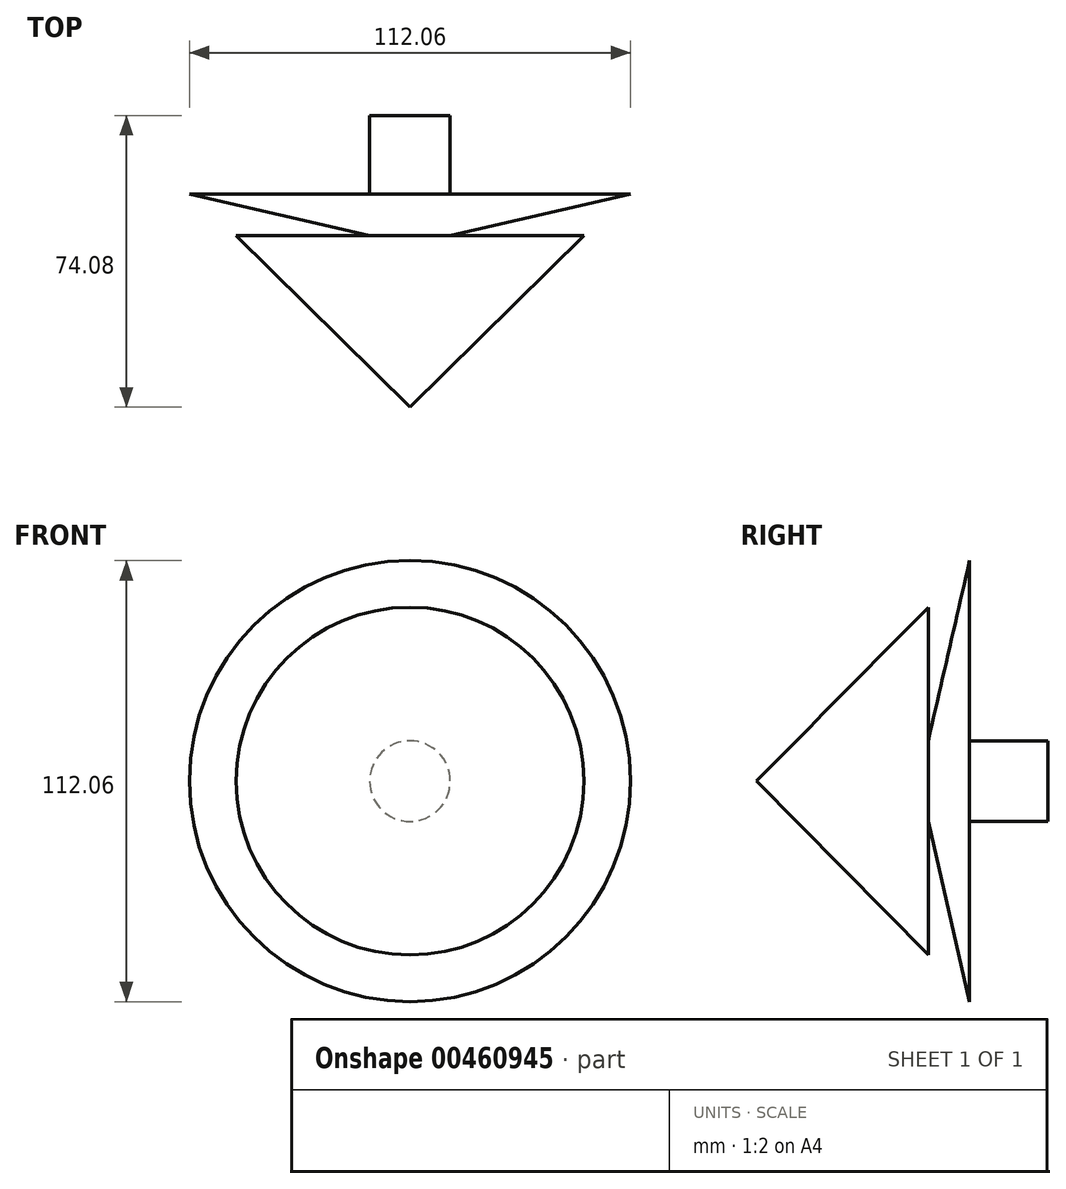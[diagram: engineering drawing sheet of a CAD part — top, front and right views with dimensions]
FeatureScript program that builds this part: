
annotation { "Feature Type Name" : "Feature", "Feature Type Description" : "" }
export const myFeature = defineFeature(function(context is Context, id is Id, definition is map)
    precondition{}
    {
        {
            var Q0;
            Q0=qCreatedBy(makeId("Top.planeOp"),FACE);
            var sketch = newSketch(context, id + "F0", { "sketchPlane" : qUnion([Q0])});
            skLineSegment(sketch, "E0", {"start": v(0, 59.54) * mm, "end": v(0, -43.64) * mm});
            skLineSegment(sketch, "E1", {"start": v(-10.24, 10.5) * mm, "end": v(-10.24, 30.44) * mm});
            skLineSegment(sketch, "E2", {"start": v(-10.24, 30.44) * mm, "end": v(0, 30.44) * mm});
            skPoint(sketch, "E3.end.orphan", {"position": v(-65.88, 30.44) * mm});
            skPoint(sketch, "E4.end.orphan", {"position": v(-26.13, 0) * mm});
            skLineSegment(sketch, "E5", {"start": v(-10.24, 10.5) * mm, "end": v(-56.03, 10.5) * mm});
            skLineSegment(sketch, "E6", {"start": v(-56.03, 10.5) * mm, "end": v(-10.24, 0) * mm});
            skLineSegment(sketch, "E7", {"start": v(-10.24, 0) * mm, "end": v(-44.18, 0) * mm});
            skLineSegment(sketch, "E8", {"start": v(-44.18, 0) * mm, "end": v(0, -43.64) * mm});
            skSolve(sketch);
        }
        {
            var Q0;
            Q0 = qSketchRegion(id + "F0", true);
            var Q1;
            Q1=sQuery(id+"F0.wireOp",EDGE,"E0");
            revolve(context, id + "F1", {"entities" : qUnion([Q0]), "axis" : qUnion([Q1]), "revolveType" : RevolveType.FULL});
        }
    });
